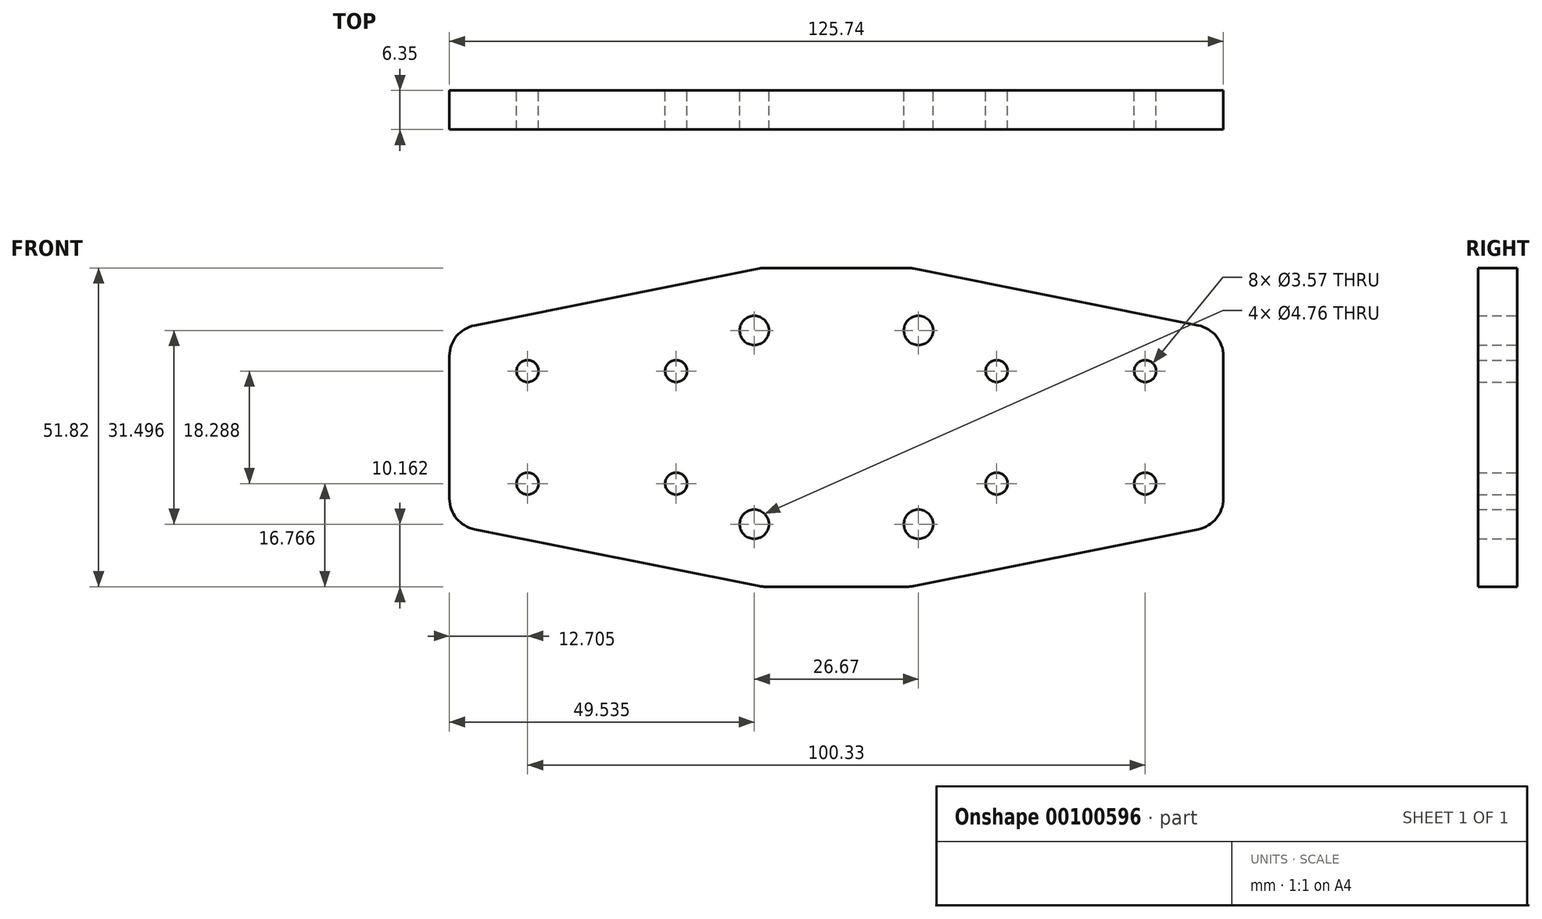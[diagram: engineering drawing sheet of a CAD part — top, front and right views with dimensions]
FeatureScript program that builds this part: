
annotation { "Feature Type Name" : "Feature", "Feature Type Description" : "" }
export const myFeature = defineFeature(function(context is Context, id is Id, definition is map)
    precondition{}
    {
        {
            var Q0;
            Q0=qCreatedBy(makeId("Front.planeOp"),FACE);
            var sketch = newSketch(context, id + "F0", { "sketchPlane" : qUnion([Q0])});
            skLineSegment(sketch, "E0.bottom", {"start": v(62.87, 25.9) * mm, "end": v(-62.87, 25.9) * mm});
            skLineSegment(sketch, "E0.top", {"start": v(62.87, -25.9) * mm, "end": v(-62.87, -25.9) * mm});
            skLineSegment(sketch, "E0.left", {"start": v(62.87, 25.9) * mm, "end": v(62.87, -25.9) * mm});
            skLineSegment(sketch, "E0.right", {"start": v(-62.87, 25.9) * mm, "end": v(-62.87, -25.9) * mm});
            skPoint(sketch, "E0.middle", {"position": v(0, 0) * mm});
            skPoint(sketch, "E1", {"position": v(13.34, 15.75) * mm});
            skPoint(sketch, "E2", {"position": v(26.04, 9.14) * mm});
            skPoint(sketch, "E3", {"position": v(50.16, 9.14) * mm});
            skPoint(sketch, "E4.MirrorP", {"position": v(-13.34, 15.75) * mm});
            skPoint(sketch, "E5.MirrorP", {"position": v(-26.04, 9.14) * mm});
            skPoint(sketch, "E6.MirrorP", {"position": v(-50.16, 9.14) * mm});
            skPoint(sketch, "E7.MirrorP", {"position": v(-50.16, -9.14) * mm});
            skPoint(sketch, "E8.MirrorP", {"position": v(-26.04, -9.14) * mm});
            skPoint(sketch, "E9.MirrorP", {"position": v(-13.34, -15.75) * mm});
            skPoint(sketch, "E10.MirrorP", {"position": v(13.34, -15.75) * mm});
            skPoint(sketch, "E11.MirrorP", {"position": v(26.04, -9.14) * mm});
            skPoint(sketch, "E12.MirrorP", {"position": v(50.16, -9.14) * mm});
            skPoint(sketch, "E13", {"position": v(38.1, 0) * mm});
            skPoint(sketch, "E14.MirrorP", {"position": v(-38.1, 0) * mm});
            skLineSegment(sketch, "E15", {"start": v(-62.87, 15.75) * mm, "end": v(-12.07, 25.9) * mm});
            skLineSegment(sketch, "E16.MirrorCS", {"start": v(62.87, 15.75) * mm, "end": v(12.06, 25.9) * mm});
            skLineSegment(sketch, "E17.MirrorCS", {"start": v(62.87, -15.75) * mm, "end": v(12.07, -25.9) * mm});
            skLineSegment(sketch, "E18.MirrorCS", {"start": v(-62.87, -15.75) * mm, "end": v(-12.06, -25.9) * mm});
            skSolve(sketch);
        }
        {
            var Q0;
            {var subQ0=sQuery(id+"F0.wireOp",EDGE,"E16.MirrorCS");var subQ1=sQuery(id+"F0.wireOp",EDGE,"E0.left");var subQ2=makeQuery(id+"F0.imprint","INTERSECT",VERTEX,{"derivedFrom":[subQ1,subQ0]});Q0=makeQuery(id+"F0.imprint","IMPRINT",FACE,{"disambiguationData":[TD([[makeQuery(id+"F0.imprint","IMPRINT",EDGE,{"disambiguationData":[TD([[subQ2,-1.0]])],"derivedFrom":subQ1}),-1.0]])]});}
            extrude(context, id + "F1", {"entities" : qUnion([Q0]), "depth" : 6.35 * mm});
        }
        {
            var Q0;
            Q0=sQuery(id+"F0.wireOp",VERTEX,"E4.MirrorP");
            var Q1;
            Q1=sQuery(id+"F0.wireOp",VERTEX,"E1");
            var Q2;
            Q2=sQuery(id+"F0.wireOp",VERTEX,"E10.MirrorP");
            var Q3;
            Q3=sQuery(id+"F0.wireOp",VERTEX,"E9.MirrorP");
            var Q4;
            Q4=makeQuery(id+"F1.opExtrude","SWEPT_BODY",BODY,{"disambiguationData":[OSD([sQuery(id+"F0.wireOp",EDGE,"E0.bottom"),sQuery(id+"F0.wireOp",EDGE,"E0.top"),sQuery(id+"F0.wireOp",EDGE,"E0.left"),sQuery(id+"F0.wireOp",EDGE,"E0.right")])]});
            hole(context, id + "F2", {"style" : HoleStyle.SIMPLE, "endStyle" : HoleEndStyle.THROUGH, "oppositeDirection" : true, "holeDiameter" : 4.76 * mm, "locations" : qUnion([Q0, Q1, Q2, Q3]), "scope" : qUnion([Q4]), "isTappedThrough" : true});
        }
        {
            var Q0;
            Q0=sQuery(id+"F0.wireOp",VERTEX,"E2");
            var Q1;
            Q1=sQuery(id+"F0.wireOp",VERTEX,"E3");
            var Q2;
            Q2=sQuery(id+"F0.wireOp",VERTEX,"E12.MirrorP");
            var Q3;
            Q3=sQuery(id+"F0.wireOp",VERTEX,"E11.MirrorP");
            var Q4;
            Q4=sQuery(id+"F0.wireOp",VERTEX,"E8.MirrorP");
            var Q5;
            Q5=sQuery(id+"F0.wireOp",VERTEX,"E5.MirrorP");
            var Q6;
            Q6=sQuery(id+"F0.wireOp",VERTEX,"E6.MirrorP");
            var Q7;
            Q7=sQuery(id+"F0.wireOp",VERTEX,"E7.MirrorP");
            var Q8;
            Q8=makeQuery(id+"F1.opExtrude","SWEPT_BODY",BODY,{"disambiguationData":[OSD([sQuery(id+"F0.wireOp",EDGE,"E0.bottom"),sQuery(id+"F0.wireOp",EDGE,"E0.top"),sQuery(id+"F0.wireOp",EDGE,"E0.left"),sQuery(id+"F0.wireOp",EDGE,"E0.right")])]});
            hole(context, id + "F3", {"style" : HoleStyle.SIMPLE, "endStyle" : HoleEndStyle.THROUGH, "oppositeDirection" : true, "holeDiameter" : 3.57 * mm, "locations" : qUnion([Q0, Q1, Q2, Q3, Q4, Q5, Q6, Q7]), "scope" : qUnion([Q8]), "isTappedThrough" : true});
        }
        {
            var Q0;
            Q0=makeQuery(id+"F1.opExtrude","SWEPT_EDGE",EDGE,{"disambiguationData":[OSD([sQuery(id+"F0.wireOp",EDGE,"E0.right"),sQuery(id+"F0.wireOp",EDGE,"E15")])]});
            var Q1;
            Q1=makeQuery(id+"F1.opExtrude","SWEPT_EDGE",EDGE,{"disambiguationData":[OSD([sQuery(id+"F0.wireOp",EDGE,"E0.left"),sQuery(id+"F0.wireOp",EDGE,"E17.MirrorCS")])]});
            var Q2;
            Q2=makeQuery(id+"F1.opExtrude","SWEPT_EDGE",EDGE,{"disambiguationData":[OSD([sQuery(id+"F0.wireOp",EDGE,"E0.left"),sQuery(id+"F0.wireOp",EDGE,"E17.MirrorCS")])]});
            var Q3;
            Q3=makeQuery(id+"F1.opExtrude","SWEPT_EDGE",EDGE,{"disambiguationData":[OSD([sQuery(id+"F0.wireOp",EDGE,"E0.right"),sQuery(id+"F0.wireOp",EDGE,"E18.MirrorCS")])]});
            var Q4;
            Q4=makeQuery(id+"F1.opExtrude","SWEPT_EDGE",EDGE,{"disambiguationData":[OSD([sQuery(id+"F0.wireOp",EDGE,"E0.right"),sQuery(id+"F0.wireOp",EDGE,"E18.MirrorCS")])]});
            var Q5;
            Q5=makeQuery(id+"F1.opExtrude","SWEPT_EDGE",EDGE,{"disambiguationData":[OSD([sQuery(id+"F0.wireOp",EDGE,"E0.right"),sQuery(id+"F0.wireOp",EDGE,"E15")])]});
            var Q6;
            Q6=makeQuery(id+"F1.opExtrude","SWEPT_EDGE",EDGE,{"disambiguationData":[OSD([sQuery(id+"F0.wireOp",EDGE,"E17.MirrorCS"),sQuery(id+"F0.wireOp",EDGE,"E18.MirrorCS")])]});
            var Q7;
            Q7=makeQuery(id+"F1.opExtrude","SWEPT_EDGE",EDGE,{"disambiguationData":[OSD([sQuery(id+"F0.wireOp",EDGE,"E15"),sQuery(id+"F0.wireOp",EDGE,"E16.MirrorCS")])]});
            fillet(context, id + "F4", {"entities" : qUnion([Q0, Q1, Q2, Q3, Q4, Q5, Q6, Q7]), "radius" : 5.08 * mm, "tangentPropagation" : true, "allowEdgeOverflow" : false});
        }
    });
